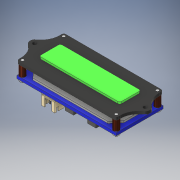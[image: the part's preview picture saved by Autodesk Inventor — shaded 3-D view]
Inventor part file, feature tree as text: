
AUTODESK INVENTOR PART (.ipt)
format: ipt  version: 2019.4 (Build 234330000, 330)  size: 1,609,728 bytes
history: native  units: mm
features: extrude x14, sketch x5, fillet x2, other x2, plane x1, chamfer x1
ambient origin geometry x8: Origin, YZ Plane, XZ Plane, XY Plane, X Axis, Y Axis, Z Axis, Center Point
bodies: Solid1 (feature_tree)
feature tree (25):
  sketch  "Sketch1"  dims[d0=25.0mm d1=53.0mm]
  extrude  "Extrusion1"  Depth=53.0mm
  extrude  "Extrusion2"  Depth=3.0mm
  fillet  "Fillet1"  Radius=2.5mm
  extrude  "Extrusion3"  Depth=43.0mm
  extrude  "Extrusion4"  Depth=1.0mm
  plane  "Work Plane1"
  sketch  "Sketch4"  dims[d40=10.0mm d45=43.0mm]
  extrude  "Extrusion5"  Depth=0.5mm TaperAngle=0.0deg
  extrude  "Extrusion6"  Depth=0.5mm TaperAngle=0.0deg
  extrude  "Extrusion8"  Depth=0.5mm
  fillet  "Fillet3"  Radius=1.5mm
  extrude  "Extrusion12"  Depth=0.5mm
  extrude  "Extrusion7"  Depth=0.5mm
  extrude  "Extrusion14"  Depth=0.5mm TaperAngle=0.0deg
  extrude  "Extrusion15"  Depth=0.5mm
  extrude  "Extrusion16"  Depth=0.5mm
  extrude  "Extrusion17"  Depth=0.5mm
  chamfer  "Chamfer2"  Distance=3.0mm
  extrude  "Extrusion18"  Depth=0.5mm TaperAngle=0.0deg
  other  "Image1"
  sketch  "Sketch3"  dims[d29=2.1mm d37=3.0mm d38=2.5mm]
  other  "Image2"
  sketch  "Sketch6"  dims[d46=11.3mm d47=1.0mm]
  sketch  "Sketch7"  dims[d48=1.0mm d60=1.5mm d61=0.0mm d62=1.0mm d63=0.0mm d64=1.0mm d65=1.5mm d69=1.5mm d70=1.5mm d73=0.1mm d74=0.0mm d75=3.0mm d76=3.0mm d77=3.0mm d78=3.0mm d79=8.03mm d80=0.0mm d81=-1.0mm d83=1.57mm d84=0.0mm d98=7.0mm d99=4.5mm d100=4.5mm d101=4.5mm d104=11.0mm d105=7.5mm d106=5.0mm d107=5.5mm d114=0.0mm d115=0.0mm d125=2.5mm d127=2.25mm d128=2.25mm d129=2.5mm d130=2.25mm d131=2.25mm d133=2.0mm d134=0.0mm d135=1.0mm d136=0.0mm d138=3.0mm d139=0.0mm d151=0.5mm d157=0.2mm d158=0.2mm d161=0.2mm d162=20.0mm d163=2.0mm d164=2.5mm d165=6.0mm d166=1.0mm d167=0.0mm d171=0.5mm d173=1.0mm d174=1.0mm d175=0.5mm d176=0.5mm d177=0.3mm d179=1.48mm d180=4.0mm d183=6.0mm d184=0.0mm d185=4.0mm d186=0.0mm d187=1.5mm d188=0.0mm d189=5.0mm d190=0.0mm d191=0.2mm d192=2.0mm d193=45.0deg d194=0.5mm d195=0.5mm d196=1.0mm d197=5.0mm d198=0.0mm]
